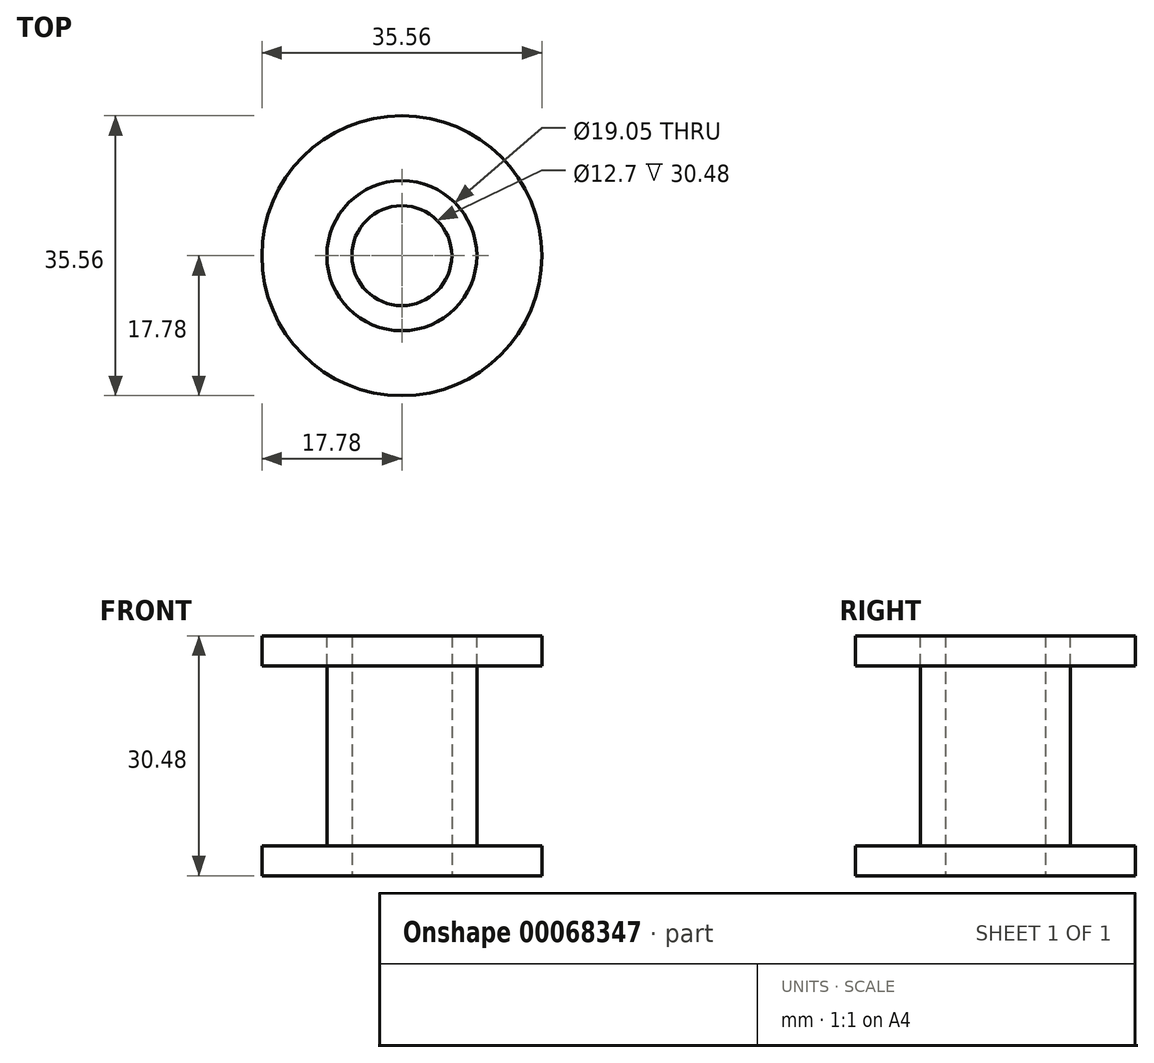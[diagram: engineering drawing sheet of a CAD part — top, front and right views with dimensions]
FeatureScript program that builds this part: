
annotation { "Feature Type Name" : "Feature", "Feature Type Description" : "" }
export const myFeature = defineFeature(function(context is Context, id is Id, definition is map)
    precondition{}
    {
        {
            var Q0;
            Q0=qCreatedBy(makeId("Top.planeOp"),FACE);
            var sketch = newSketch(context, id + "F0", { "sketchPlane" : qUnion([Q0])});
            skCircle(sketch, "E0", {"center": v(0, 0) * mm, "radius": 9.53 * mm});
            skCircle(sketch, "E1", {"center": v(0, 0) * mm, "radius": 6.35 * mm});
            skCircle(sketch, "E2", {"center": v(0, 0) * mm, "radius": 17.78 * mm});
            skSolve(sketch);
        }
        {
            var Q0;
            Q0=makeQuery(id+"F0.imprint","IMPRINT",FACE,{"disambiguationData":[TD([[makeQuery(id+"F0.imprint","IMPRINT",EDGE,{"derivedFrom":sQuery(id+"F0.wireOp",EDGE,"E0")}),-1.0]])]});
            extrude(context, id + "F1", {"entities" : qUnion([Q0]), "depth" : 3.8 * mm});
        }
        {
            var Q0;
            Q0=makeQuery(id+"F0.imprint","IMPRINT",FACE,{"disambiguationData":[TD([[makeQuery(id+"F0.imprint","IMPRINT",EDGE,{"derivedFrom":sQuery(id+"F0.wireOp",EDGE,"E0")}),1.0]])]});
            extrude(context, id + "F2", {"entities" : qUnion([Q0]), "operationType" : NewBodyOperationType.ADD, "depth" : 30.48 * mm});
        }
        {
            var Q0;
            Q0=makeQuery(id+"F2.opExtrude","CAP_FACE",FACE,{"disambiguationData":[OSD([sQuery(id+"F0.wireOp",EDGE,"E0"),sQuery(id+"F0.wireOp",EDGE,"E1")])],"isStart":false});
            var sketch = newSketch(context, id + "F3", { "sketchPlane" : qUnion([Q0])});
            skCircle(sketch, "E3", {"center": v(0, 0) * mm, "radius": 17.78 * mm});
            skSolve(sketch);
        }
        {
            var Q0;
            Q0=makeQuery(id+"F3.imprint","IMPRINT",FACE,{"disambiguationData":[TD([[makeQuery(id+"F3.imprint","IMPRINT",EDGE,{"derivedFrom":sQuery(id+"F3.wireOp",EDGE,"E3")}),1.0]])]});
            extrude(context, id + "F4", {"entities" : qUnion([Q0]), "oppositeDirection" : true, "depth" : 3.8 * mm});
        }
    });
